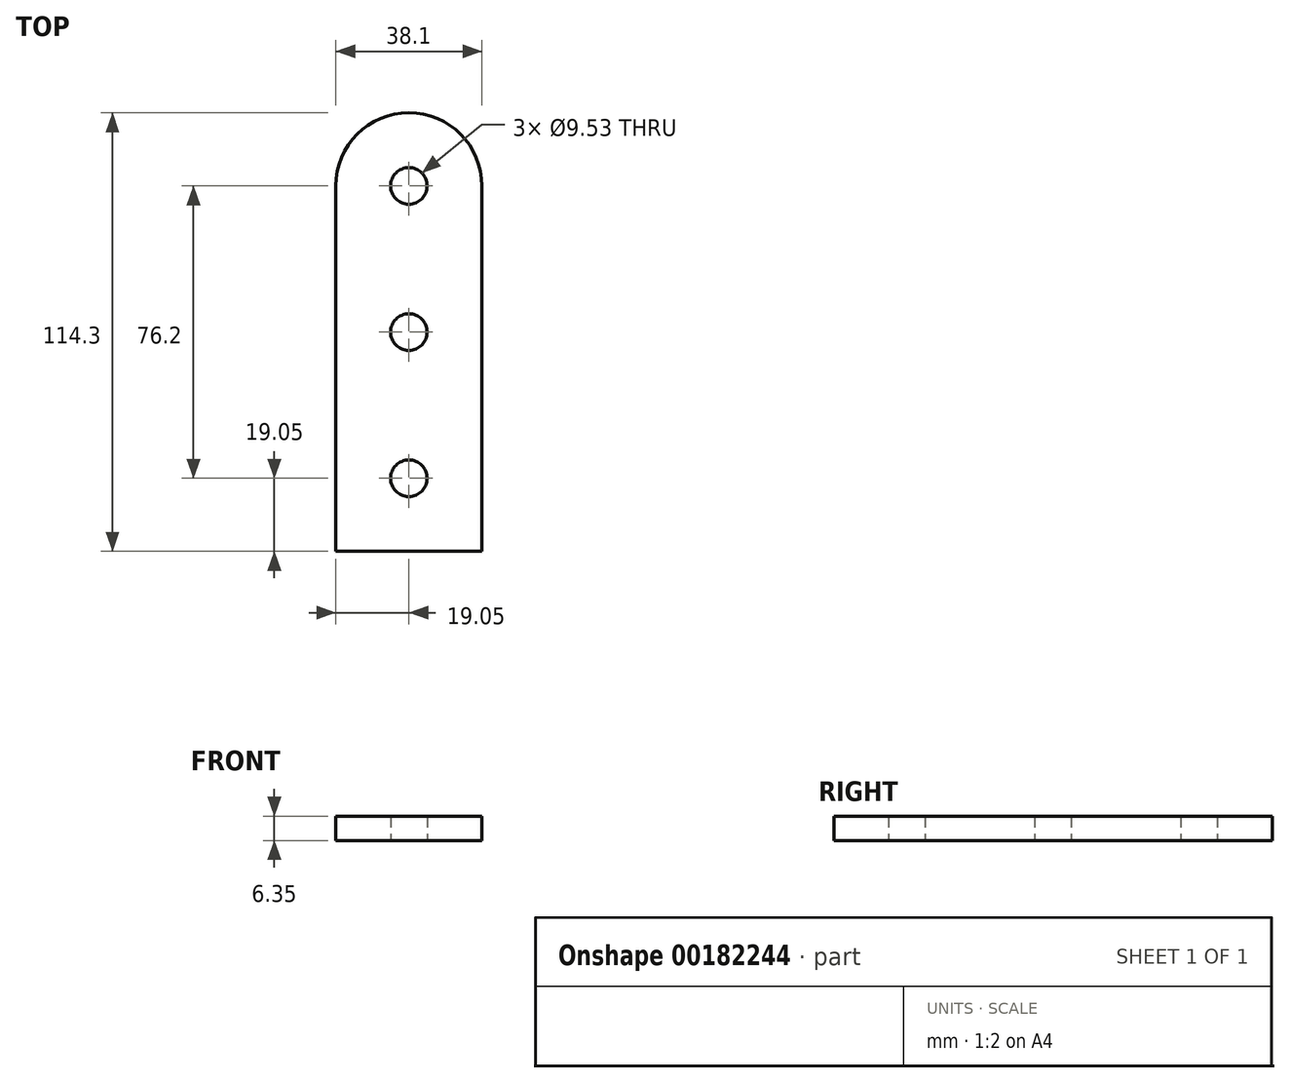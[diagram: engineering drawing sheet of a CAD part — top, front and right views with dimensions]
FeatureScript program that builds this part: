
annotation { "Feature Type Name" : "Feature", "Feature Type Description" : "" }
export const myFeature = defineFeature(function(context is Context, id is Id, definition is map)
    precondition{}
    {
        {
            var Q0;
            Q0=qCreatedBy(makeId("Top.planeOp"),FACE);
            var sketch = newSketch(context, id + "F0", { "sketchPlane" : qUnion([Q0])});
            skLineSegment(sketch, "E0.bottom", {"start": v(0, 0) * mm, "end": v(38.1, 0) * mm});
            skLineSegment(sketch, "E0.top", {"start": v(0, 95.25) * mm, "end": v(38.1, 95.25) * mm});
            skLineSegment(sketch, "E0.left", {"start": v(0, 0) * mm, "end": v(0, 95.25) * mm});
            skLineSegment(sketch, "E0.right", {"start": v(38.1, 0) * mm, "end": v(38.1, 95.25) * mm});
            skArc(sketch, "E1", {"start": v(38.1, 95.25) * mm, "mid": v(19.05, 114.3) * mm, "end": v(0, 95.25) * mm});
            skSolve(sketch);
        }
        {
            var Q0;
            Q0=qSketchRegion(id+"F0",true);
            extrude(context, id + "F1", {"entities" : qUnion([Q0]), "depth" : 6.35 * mm});
        }
        {
            var Q0;
            Q0=makeQuery(id+"F1.opExtrude","CAP_FACE",FACE,{"disambiguationData":[OSD([sQuery(id+"F0.wireOp",EDGE,"E0.bottom"),sQuery(id+"F0.wireOp",EDGE,"E0.left"),sQuery(id+"F0.wireOp",EDGE,"E0.right"),sQuery(id+"F0.wireOp",EDGE,"E1")])],"isStart":false});
            var sketch = newSketch(context, id + "F2", { "sketchPlane" : qUnion([Q0])});
            skPoint(sketch, "E2", {"position": v(19.05, 19.05) * mm});
            skPoint(sketch, "E3", {"position": v(19.05, 57.15) * mm});
            skPoint(sketch, "E4", {"position": v(19.05, 95.25) * mm});
            skSolve(sketch);
        }
        {
            var Q0;
            Q0=sQuery(id+"F2.wireOp",VERTEX,"E4");
            var Q1;
            Q1=sQuery(id+"F2.wireOp",VERTEX,"E3");
            var Q2;
            Q2=sQuery(id+"F2.wireOp",VERTEX,"E2");
            var Q3;
            Q3=makeQuery(id+"F1.opExtrude","SWEPT_BODY",BODY,{"disambiguationData":[OSD([sQuery(id+"F0.wireOp",EDGE,"E0.bottom"),sQuery(id+"F0.wireOp",EDGE,"E0.left"),sQuery(id+"F0.wireOp",EDGE,"E0.right"),sQuery(id+"F0.wireOp",EDGE,"E1")])]});
            hole(context, id + "F3", {"style" : HoleStyle.SIMPLE, "holeDiameter" : 9.52 * mm, "endStyle" : HoleEndStyle.THROUGH, "locations" : qUnion([Q0, Q1, Q2]), "scope" : qUnion([Q3])});
        }
    });
